# Revit family: Faucet-Lavatory-KOHLER-Beam-K-26042IN_1
name_source: partatom
category: Plumbing Fixtures
units: mm (PartAtom-declared; Revit-internal decimal feet)

## family parameters
Cut with Voids When Loaded = No
Host = Face
Maintain Annotation Orientation = No
OmniClass Number = 23.31.11.00
OmniClass Title = Faucets
Part Type = Normal
Room Calculation Point = No
Round Connector Dimension = Use Diameter
Shared = No

## types (1)
- CP-Polished Chrome
    ADA Compliant = No
    Assembly Code = D2010
    CW Connection = Yes
    Cold Water Inlet = Cold Water Inlet
    Date Modified = 02/10/2022
    Default Elevation = 36"
    Description = Pillar Tap
    Drain Included = No
    Finish = Kohler-Metal-CP-Polished_Chrome
    Flow Rate = 0 GPM
    HW Connection = No
    Handle Clearance = 2 1/2"
    Height = 5 3/8"
    Hot Water Inlet = Hot Water Inlet
    Length = 3 15/16"
    Manufacturer = KOHLER Co.
    Master Format 2014 = 22 41 39
    Master Format 2014 Name = Residential Faucets, Supplies, and Trim
    Material = Premium Metal Construction
    Model = K-26042IN-4-CP
    Pressure = 0.00 psi
    Product Name = Beam
    Product Page URL = https://www.kohler.co.in
    Spout Reach = 3 15/16"
    Type = 1
    URL = https://www.kohler.co.in
    Vent Connection = No
    Waste Connection = No
    Waste Water Outlet = Waste Water Outlet
    WaterSense Certified = No
    Width = 1 3/4"

## geometry (parser evidence)
native form markers: Sweep x5
no freeform markers — native parametric forms only
